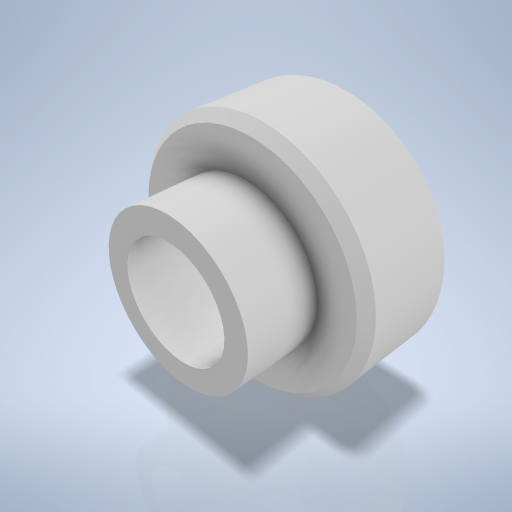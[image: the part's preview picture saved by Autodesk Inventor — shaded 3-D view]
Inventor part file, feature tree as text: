
AUTODESK INVENTOR PART (.ipt)
format: ipt  version: 2024.2 (Build 282272000, 272)  size: 274,944 bytes
history: native  units: mm
features: sketch x4, extrude x2, hole x2, chamfer x1
ambient origin geometry x8: Origin, YZ Plane, XZ Plane, XY Plane, X Axis, Y Axis, Z Axis, Center Point
bodies: Volumenkörper1 (feature_tree)
feature tree (9):
  extrude  "Extrusion1"  Depth=6.5mm TaperAngle=0.0deg
  extrude  "Extrusion2"  Depth=4.5mm TaperAngle=0.0deg
  hole  "Bohrung1"  [1 undecoded]
  hole  "Bohrung2"  [1 undecoded]
  chamfer  "Fasen1"  [1 undecoded]
  sketch  "Skizze1"  dims[d0=16.0mm d1=6.5mm d2=0.0mm]
  sketch  "Skizze2"  dims[d3=10.0mm d4=4.5mm d5=0.0mm]
  sketch  "Skizze3"  dims[d6=7.0mm d7=6.0mm d8=4.0mm d9=2.0mm d10=90.0deg d11=5.5mm d12=20.594885mm]
  sketch  "Skizze4"  dims[d13=12.0mm d14=6.0mm d15=4.0mm d16=2.0mm d17=90.0deg d18=5.0mm d19=0.0mm d20=0.6mm d21=2.0mm d22=45.0deg]
note: 3 required parameter values undecoded (feature->parameter linkage not recoverable at this tier; creation-order binding heuristic only, values carry confidence <= 0.55)
